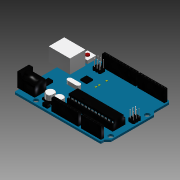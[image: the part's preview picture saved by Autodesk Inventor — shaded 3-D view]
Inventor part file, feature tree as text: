
AUTODESK INVENTOR PART (.ipt)
format: ipt  version: 2014 (Build 180170000, 170)  size: 1,527,296 bytes
history: native  units: in
note: dims shown in document units (in); Inventor stores cm internally (conversion verified against a paired STEP export)
features: sketch x39, extrude x38, fillet x15, chamfer x10, pattern_linear x8, projected_geometry x7, plane x1, mirror x1
ambient origin geometry x8: Origin, YZ Plane, XZ Plane, XY Plane, X Axis, Y Axis, Z Axis, Center Point
bodies: Solid1 (feature_tree), Body (feature_tree)
feature tree (119):
  fillet  "Board Fillets"  Radius=2.1in
  extrude  "Mount Holes"  Depth=2.6in
  extrude  "USB Body"  TaperAngle=135.0deg  [1 undecoded]
  extrude  "USB Hole"  Depth=1.3in
  extrude  "USB Center Pin"  Depth=0.06in TaperAngle=0.0deg
  extrude  "Power Plug Body 1"  Depth=0.14in
  extrude  "Power Plug Body 2"  Depth=0.05in
  extrude  "Power Plug Hole"  Depth=0.2in
  extrude  "Power Plug Pin"  Depth=0.6in
  fillet  "Power Plug Pin Rounded"  Radius=0.06in
  extrude  "Power Plug Bottom"  Depth=0.6385in
  fillet  "Power Plug Bottom Round"  Radius=0.25in
  fillet  "Power Plug Bottom Smooth"  Radius=0.35in
  fillet  "Power Plug Bottom Solder"  Radius=0.42in
  extrude  "USB Bottom"  Depth=0.05in
  fillet  "USB Bottom Round"  Radius=0.05in
  fillet  "USB Bottom Smooth"  Radius=0.05in
  fillet  "USB Bottom Solder"  [1 undecoded]
  extrude  "Pin Headers"  Depth=0.22in
  extrude  "Power Pin Group"  Depth=0.22in
  chamfer  "Power Pin Group Chamfer"  Distance=0.33in
  extrude  "Power Pin Group Bottom"  Depth=0.52in
  chamfer  "Power Pin Group Point"  Distance=0.43in
  fillet  "Power Pin Group Solder"  Radius=0.02in
  pattern_linear  "Rectangular Pattern3"  Spacing1=0.33in  [1 undecoded]
  extrude  "Analog Pin Group"  Depth=0.01in TaperAngle=45.0deg
  chamfer  "Analog Pin Group Chamfer"  Distance=0.02in
  extrude  "Analog Pin Group Bottom"  Depth=0.015in
  chamfer  "Analog Pin Group Point"  Distance=0.015in
  fillet  "Analog Pin Group Solder"  Radius=0.05in
  pattern_linear  "Rectangular Pattern4"  Spacing1=0.01in  [1 undecoded]
  extrude  "Data Pin Group 1"  Depth=0.03in
  chamfer  "Data Pin Group 1 Chamfer"  Distance=0.1in
  extrude  "Data Pin Group 1 Bottom"  Depth=0.05in
  chamfer  "Data Pin Group 1 Point"  Distance=0.02in
  fillet  "Data Pin Group 1 Solder"  Radius=0.03in
  pattern_linear  "Rectangular Pattern5"  Spacing1=0.03in  [1 undecoded]
  extrude  "Data Pin Group 2"  Depth=0.03in
  chamfer  "Data Pin Group 2 Chamfer"  Distance=0.03in
  extrude  "Data Pin Group 2 Bottom"  Depth=0.03in
  chamfer  "Data Pin Group 2 Point"  Distance=0.03in
  fillet  "Data Pin Group 2 Solder"  Radius=0.33in
  pattern_linear  "Rectangular Pattern6"  Spacing1=0.01in  [1 undecoded]
  extrude  "Microprocessor Socket"  Depth=0.02in
  extrude  "Microprocessor"  Depth=0.05in TaperAngle=0.0deg
  extrude  "Microprocessor Pins"  Depth=0.01in TaperAngle=45.0deg
  pattern_linear  "Rectangular Pattern7"  Spacing1=0.03in  [1 undecoded]
  extrude  "Microprocessor End Pins"  Depth=0.1in
  plane  "Work Plane1"
  mirror  "Mirror1"
  extrude  "ICSP Pin Base"  Depth=0.03in
  extrude  "ICSP Pin"  Depth=0.03in
  pattern_linear  "Rectangular Pattern8"  Spacing1=0.03in  [1 undecoded]
  extrude  "AREF Pin Base"  Depth=0.03in
  extrude  "AREF Pin"  Depth=0.33in TaperAngle=0.0deg
  pattern_linear  "Rectangular Pattern9"  Spacing1=0.01in  [1 undecoded]
  extrude  "Reset Button Base"  Depth=0.02in
  extrude  "Reset Button"  Depth=0.05in TaperAngle=0.0deg
  extrude  "Extrusion31"  Depth=0.01in TaperAngle=45.0deg
  extrude  "Extrusion32"  Depth=0.03in
  fillet  "Fillet13"  Radius=0.1in
  extrude  "Extrusion33"  Depth=0.03in
  extrude  "Extrusion34"  Depth=0.03in
  extrude  "Extrusion35"  Depth=0.03in
  extrude  "Extrusion36"  Depth=0.03in
  extrude  "Extrusion37"  Depth=0.33in TaperAngle=0.0deg
  extrude  "Extrusion38"  Depth=0.02in
  chamfer  "Chamfer9"  Distance=0.05in
  fillet  "Fillet14"  Radius=0.01in
  extrude  "Extrusion39"  Depth=0.03in
  chamfer  "Chamfer10"  Distance=0.01in Angle=45.0deg
  fillet  "Fillet15"  Radius=0.1in
  pattern_linear  "Rectangular Pattern10"  Spacing1=0.1in  [1 undecoded]
  sketch  "Sketch1"  dims[d2=2.7in d3=2.6in]
  sketch  "Sketch2"  dims[d4=0.05in d5=135.0deg]
  sketch  "Sketch3"  dims[d6=0.6in d7=1.3in]
  sketch  "Sketch4"  dims[d8=135.0deg d9=0.06in d10=0.0in]
  sketch  "Sketch5"  dims[d11=0.025in d12=0.14in]
  sketch  "Sketch6"  dims[d13=2.0in d14=0.05in]
  sketch  "Sketch7"  dims[d15=0.1in d16=0.2in]
  sketch  "Sketch8"  dims[d17=1.1in d18=0.6in d19=0.06in d20=0.0in]
  sketch  "Sketch9"  dims[d21=0.4665in d22=0.6385in d23=0.25in d24=0.35in d25=0.42in d26=0.0in]
  sketch  "Sketch10"  dims[d27=0.05in d28=0.05in d29=0.05in d30=0.05in d31=135.0deg]
  sketch  "Sketch11"  dims[d32=135.0deg d33=0.22in]
  sketch  "Sketch12"  dims[d34=0.35in d35=0.0in d36=0.22in]
  projected_geometry  "Projected Loop1"
  sketch  "Sketch13"  dims[d37=0.12in]
  projected_geometry  "Projected Loop2"
  sketch  "Sketch14"  dims[d38=0.1in d39=0.33in d40=0.0in]
  projected_geometry  "Projected Loop3"
  sketch  "Sketch15"  dims[d41=0.35in d42=0.52in]
  sketch  "Sketch16"  dims[d43=0.15in]
  projected_geometry  "Projected Loop4"
  sketch  "Sketch17"  dims[d44=0.06in d45=0.43in d46=0.0in d47=0.02in]
  sketch  "Sketch18"  dims[d48=0.4in d49=0.0in]
  projected_geometry  "Projected Loop5"
  sketch  "Sketch19"  dims[d50=0.25in]
  sketch  "Sketch20"  dims[d51=0.0425in]
  sketch  "Sketch21"  dims[d52=0.39in d53=0.0in]
  sketch  "Sketch22"  dims[d54=0.05in]
  sketch  "Sketch23"  dims[d55=0.32in d56=0.0in]
  sketch  "Sketch24"  dims[d57=0.025in]
  sketch  "Sketch25"  dims[d58=0.09in]
  sketch  "Sketch26"  dims[d59=0.81in]
  sketch  "Sketch27"  dims[d60=0.085in]
  sketch  "Sketch28"  dims[d61=0.6in]
  sketch  "Sketch29"  dims[d62=0.6in]
  sketch  "Sketch30"  dims[d63=0.05in]
  sketch  "Sketch31"  dims[d64=0.82in]
  sketch  "Sketch32"  dims[d65=0.05in]
  projected_geometry  "Projected Loop6"
  sketch  "Sketch33"  dims[d66=1.01in]
  sketch  "Sketch34"  dims[d67=0.05in]
  sketch  "Sketch35"  dims[d68=0.35in d69=0.0in]
  sketch  "Sketch36"  dims[d70=0.03in]
  sketch  "Sketch37"  dims[d71=0.03in]
  sketch  "Sketch38"  dims[d72=0.03in]
  sketch  "Sketch39"  dims[d73=0.03in d74=0.33in d75=0.0in d76=0.01in d77=0.125in d78=45.0deg d85=0.02in d86=0.015in d87=0.015in d88=0.05in d89=0.0in d90=0.01in d91=0.125in d92=45.0deg d93=0.03in d94=3.1496in d96=0.1in d97=0.05in d98=0.02in d99=0.03in d100=0.03in d101=0.03in d102=0.03in d103=0.03in d104=0.03in d105=0.33in d106=0.0in d107=0.01in d108=0.125in d109=45.0deg d110=0.02in d111=0.05in d112=0.0in d113=0.01in d114=0.125in d115=45.0deg d116=0.03in d117=2.3622in d119=0.1in d120=0.03in d121=0.03in d122=0.03in d123=0.03in d124=0.33in d125=0.0in d126=0.01in d127=0.125in d128=45.0deg d129=0.02in d130=0.05in d131=0.0in d132=0.01in d133=0.125in d134=45.0deg d135=0.03in d136=3.1496in d138=0.1in d139=0.03in d140=0.03in d141=0.03in d142=0.03in d143=0.33in d144=0.0in d145=0.02in d146=0.05in d147=0.0in d148=0.01in d149=0.125in d150=45.0deg d151=0.03in d152=0.01in d153=0.125in d154=45.0deg d155=3.937in d157=0.1in d158=0.1in d159=0.02in d160=0.25in d161=0.28in d162=0.23in d163=0.36in d164=0.11in d165=0.1in d166=0.0in d167=0.05in d168=0.005in d169=0.05in d170=0.01in d171=0.06in d172=0.48in d173=0.0067in d174=0.0067in d175=0.135in d176=0.1in d177=0.0in d178=0.025in d179=0.005in d180=0.025in d181=0.38in d182=1.38in d183=0.3in d184=0.18in d185=0.18in d186=0.0in d187=0.275in d188=0.0525in d189=0.0525in d190=0.1in d191=0.0in d192=0.065in d193=0.04in d194=0.124in d195=0.01in d196=0.0in d197=4.7244in d199=0.1in d200=0.0325in d202=0.0325in d203=0.01in d204=0.0in d205=-0.1875in d206=0.04in d207=0.185in d208=0.05in d209=0.12in d210=0.08in d211=0.0in d212=0.02in d213=0.23in d214=0.0in d215=1.1811in d217=0.08in d218=0.04in d219=0.185in d220=0.04in d221=0.185in d223=0.13in d224=0.08in d225=0.0in d226=0.02in d227=0.23in d228=0.0in d229=1.1811in d231=0.08in d232=0.26in d233=0.26in d234=0.02in d235=0.12in d236=0.1in d237=0.0in d238=0.11in d239=0.03in d240=0.0in d241=0.25in d242=0.02in d243=0.21in d244=0.05in d245=0.0in d246=0.16in d247=0.0in d248=0.025in d249=0.15in d250=0.1in d251=0.05in d252=0.12in d253=0.09in d254=0.0in d255=0.065in d256=0.38in d257=0.55in d258=0.62in d259=0.11in d260=0.0in d261=0.19in d262=0.19in d263=0.17in d264=0.31in d265=0.04in d266=0.0in d267=0.05in d268=0.04in d269=0.2675in d270=0.173in d271=0.05in d272=0.2in d273=0.01in d274=0.0in d275=0.13in d276=0.21in d277=0.465in d278=0.21in d279=0.065in d280=0.0in d281=0.05in d282=0.0in d283=0.01in d284=0.125in d285=45.0deg d286=0.02in d288=0.37in d289=0.05in d290=0.0in d291=0.01in d292=0.125in d293=45.0deg d294=0.03in d295=5.5118in d297=0.1025in d298=0.7874in d300=0.25in]
  projected_geometry  "Projected Loop7"
note: 10 required parameter values undecoded (feature->parameter linkage not recoverable at this tier; creation-order binding heuristic only, values carry confidence <= 0.55)
